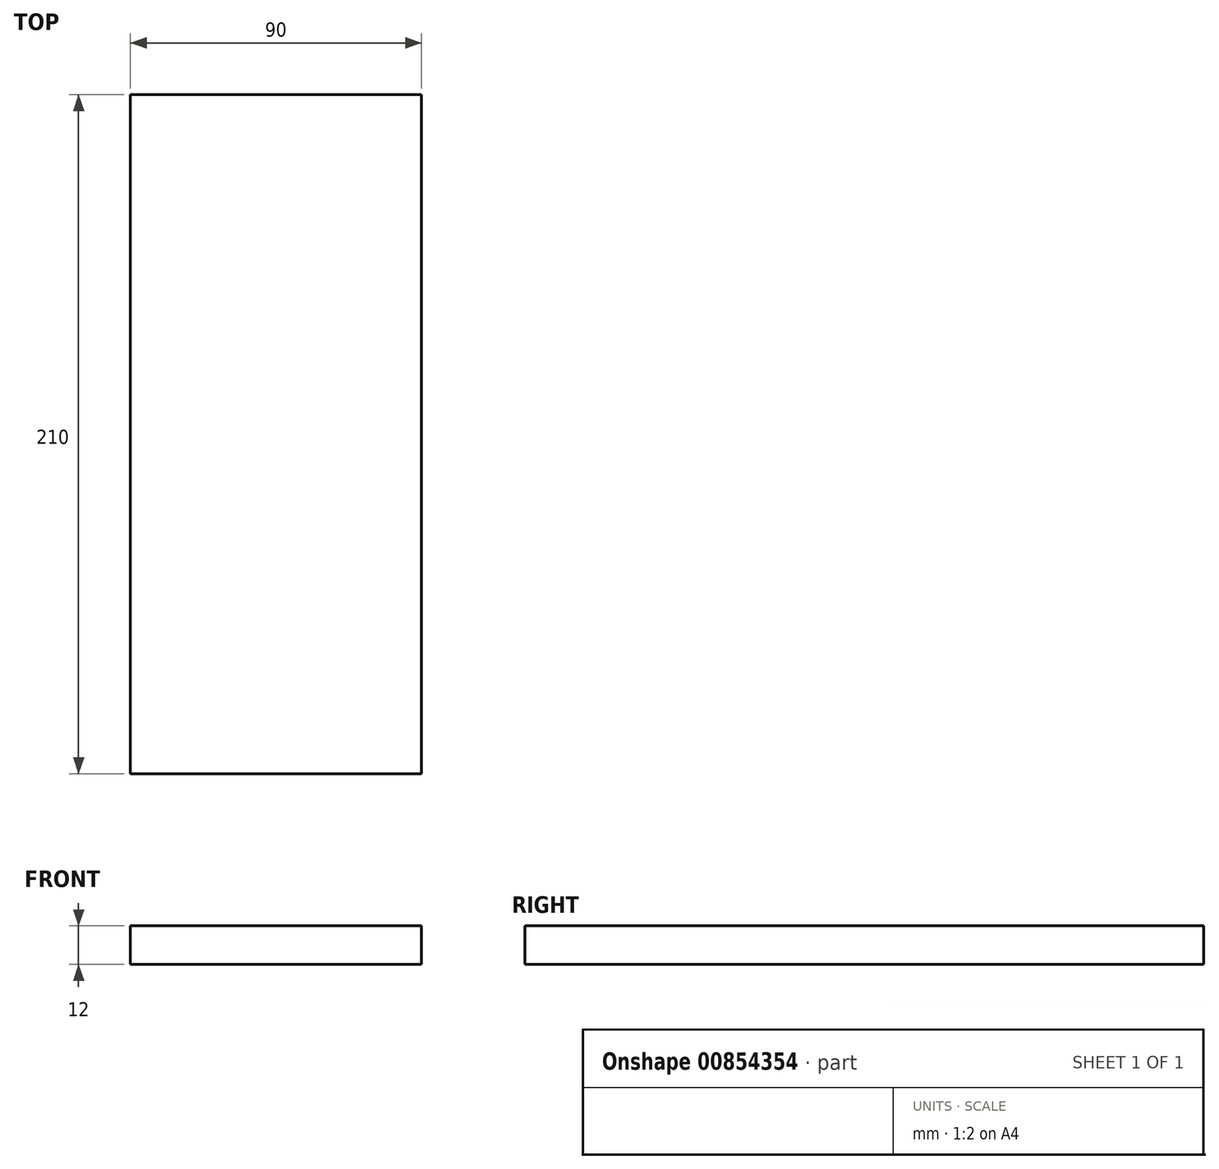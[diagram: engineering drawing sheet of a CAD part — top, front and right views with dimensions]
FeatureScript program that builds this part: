
annotation { "Feature Type Name" : "Feature", "Feature Type Description" : "" }
export const myFeature = defineFeature(function(context is Context, id is Id, definition is map)
    precondition{}
    {
        {
            var Q0;
            Q0=qCreatedBy(makeId("Top.planeOp"),FACE);
            var sketch = newSketch(context, id + "F0", { "sketchPlane" : qUnion([Q0])});
            skLineSegment(sketch, "E0.bottom", {"start": v(-45, 105) * mm, "end": v(45, 105) * mm});
            skLineSegment(sketch, "E0.top", {"start": v(-45, -105) * mm, "end": v(45, -105) * mm});
            skLineSegment(sketch, "E0.left", {"start": v(-45, 105) * mm, "end": v(-45, -105) * mm});
            skLineSegment(sketch, "E0.right", {"start": v(45, 105) * mm, "end": v(45, -105) * mm});
            skPoint(sketch, "E0.middle", {"position": v(0, 0) * mm});
            skSolve(sketch);
        }
        {
            var Q0;
            Q0 = qSketchRegion(id + "F0", true);
            extrude(context, id + "F1", {"entities" : qUnion([Q0]), "depth" : 12 * mm, "offsetDistance" : 25.4 * mm});
        }
    });
